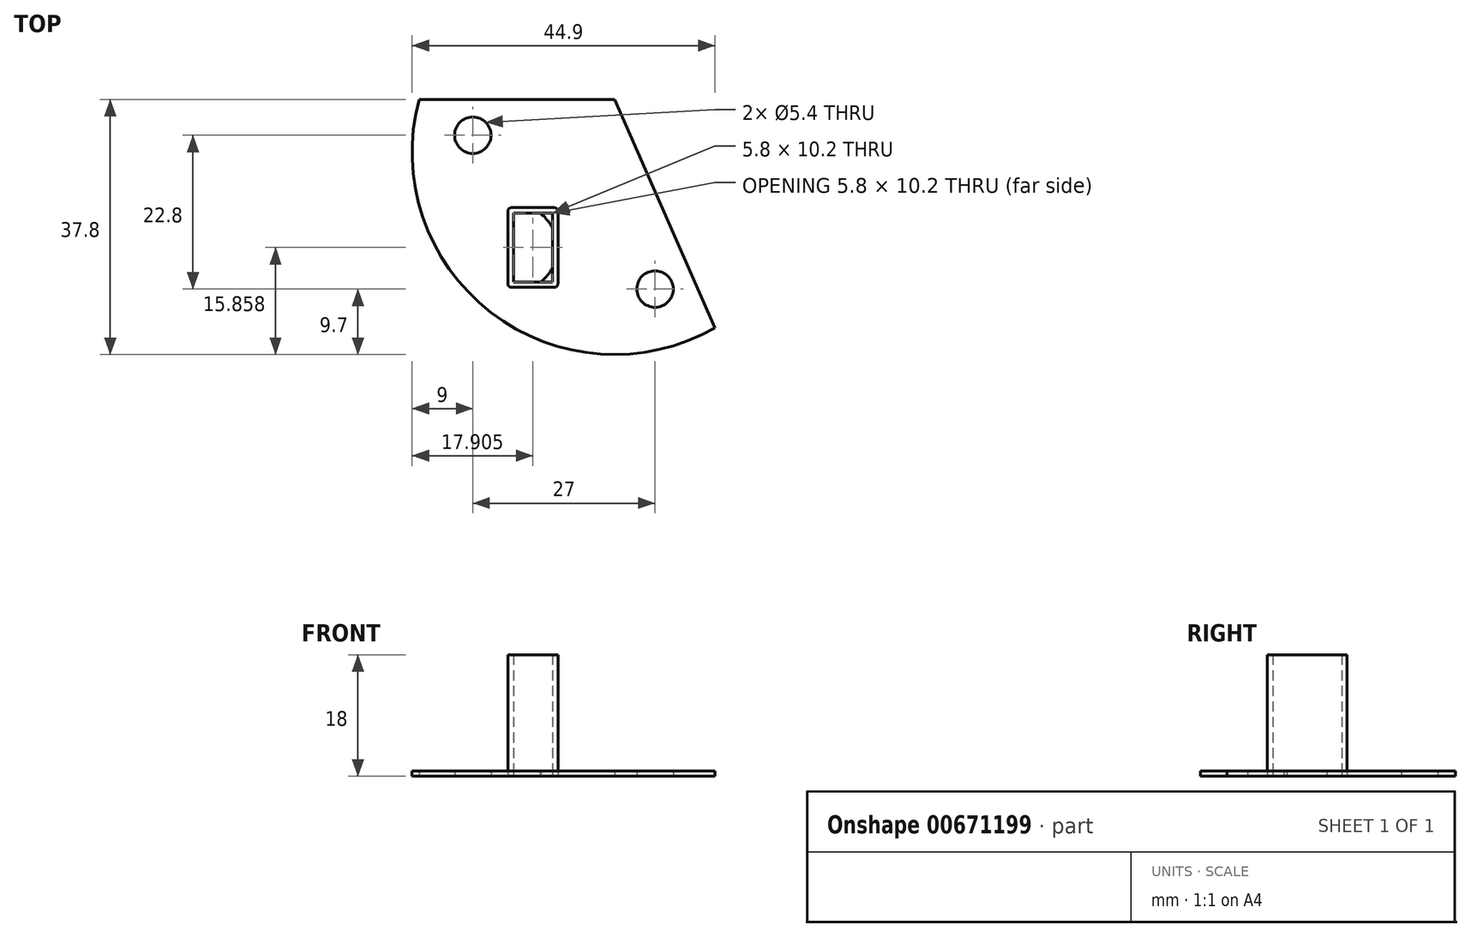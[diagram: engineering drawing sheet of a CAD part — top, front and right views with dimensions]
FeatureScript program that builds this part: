
annotation { "Feature Type Name" : "Feature", "Feature Type Description" : "" }
export const myFeature = defineFeature(function(context is Context, id is Id, definition is map)
    precondition{}
    {
        {
            var Q0;
            Q0=qCreatedBy(makeId("Top.planeOp"),FACE);
            var sketch = newSketch(context, id + "F0", { "sketchPlane" : qUnion([Q0])});
            skArc(sketch, "E0", {"start": v(-28.97, 7.8) * mm, "mid": v(-18.32, -23.75) * mm, "end": v(14.9, -26.04) * mm});
            skCircle(sketch, "E1", {"center": v(-21, 2.5) * mm, "radius": 2.7 * mm});
            skCircle(sketch, "E2", {"center": v(6, -20.3) * mm, "radius": 2.7 * mm});
            skCircle(sketch, "E3", {"center": v(-15, -14.2) * mm, "radius": 6.5 * mm});
            skLineSegment(sketch, "E4", {"start": v(-28.97, 7.8) * mm, "end": v(0, 7.8) * mm});
            skLineSegment(sketch, "E5", {"start": v(0, 7.8) * mm, "end": v(14.9, -26.04) * mm});
            skLineSegment(sketch, "E6.bottom", {"start": v(-15, -9.04) * mm, "end": v(-9.2, -9.04) * mm});
            skLineSegment(sketch, "E6.top", {"start": v(-15, -19.24) * mm, "end": v(-9.2, -19.24) * mm});
            skLineSegment(sketch, "E6.left", {"start": v(-15, -9.04) * mm, "end": v(-15, -19.24) * mm});
            skLineSegment(sketch, "E6.right", {"start": v(-9.2, -9.04) * mm, "end": v(-9.2, -19.24) * mm});
            skLineSegment(sketch, "E7.0", {"start": v(-8.4, -8.74) * mm, "end": v(-8.4, -19.54) * mm});
            skLineSegment(sketch, "E7.1", {"start": v(-15.3, -8.24) * mm, "end": v(-8.9, -8.24) * mm});
            skLineSegment(sketch, "E7.2", {"start": v(-15.8, -8.74) * mm, "end": v(-15.8, -19.54) * mm});
            skLineSegment(sketch, "E7.3", {"start": v(-15.3, -20.04) * mm, "end": v(-8.9, -20.04) * mm});
            skPoint(sketch, "E8.visualSharp", {"position": v(-15.8, -8.24) * mm});
            skArc(sketch, "E8.filletArc", {"start": v(-15.3, -8.24) * mm, "mid": v(-15.65, -8.39) * mm, "end": v(-15.8, -8.74) * mm});
            skPoint(sketch, "E9.visualSharp", {"position": v(-15.8, -20.04) * mm});
            skArc(sketch, "E9.filletArc", {"start": v(-15.8, -19.54) * mm, "mid": v(-15.65, -19.9) * mm, "end": v(-15.3, -20.04) * mm});
            skPoint(sketch, "E10.visualSharp", {"position": v(-8.4, -20.04) * mm});
            skArc(sketch, "E10.filletArc", {"start": v(-8.9, -20.04) * mm, "mid": v(-8.54, -19.9) * mm, "end": v(-8.4, -19.54) * mm});
            skPoint(sketch, "E11.visualSharp", {"position": v(-8.4, -8.24) * mm});
            skArc(sketch, "E11.filletArc", {"start": v(-8.4, -8.74) * mm, "mid": v(-8.54, -8.39) * mm, "end": v(-8.9, -8.24) * mm});
            skSolve(sketch);
        }
        {
            var Q0;
            Q0=makeQuery(id+"F0.imprint","IMPRINT",FACE,{"disambiguationData":[TD([[makeQuery(id+"F0.imprint","IMPRINT",EDGE,{"derivedFrom":sQuery(id+"F0.wireOp",EDGE,"E0")}),1.0]])]});
            var Q1;
            Q1=makeQuery(id+"F0.imprint","IMPRINT",FACE,{"disambiguationData":[TD([[makeQuery(id+"F0.imprint","IMPRINT",EDGE,{"derivedFrom":sQuery(id+"F0.wireOp",EDGE,"E7.2")}),-1.0]])]});
            var Q2;
            {var subQ0=sQuery(id+"F0.wireOp",EDGE,"E6.left");Q2=makeQuery(id+"F0.imprint","IMPRINT",FACE,{"disambiguationData":[TD([[makeQuery(id+"F0.imprint","IMPRINT",EDGE,{"derivedFrom":subQ0}),-1.0]])]});}
            var Q3;
            Q3=makeQuery(id+"F0.imprint","IMPRINT",FACE,{"disambiguationData":[TD([[makeQuery(id+"F0.imprint","IMPRINT",EDGE,{"derivedFrom":sQuery(id+"F0.wireOp",EDGE,"E7.0")}),-1.0]])]});
            var Q4;
            {var subQ0=sQuery(id+"F0.wireOp",EDGE,"E6.bottom");var subQ1=sQuery(id+"F0.wireOp",EDGE,"E3");var subQ2=makeQuery(id+"F0.imprint","INTERSECT",VERTEX,{"derivedFrom":[subQ1,subQ0]});Q4=makeQuery(id+"F0.imprint","IMPRINT",FACE,{"disambiguationData":[TD([[makeQuery(id+"F0.imprint","IMPRINT",EDGE,{"disambiguationData":[TD([[subQ2,1.0]])],"derivedFrom":subQ1}),-1.0]])]});}
            var Q5;
            {var subQ0=sQuery(id+"F0.wireOp",EDGE,"E6.right");var subQ1=sQuery(id+"F0.wireOp",EDGE,"E3");var subQ2=makeQuery(id+"F0.imprint","INTERSECT",VERTEX,{"disambiguationData":[OD(0.0)],"derivedFrom":[subQ1,subQ0]});Q5=makeQuery(id+"F0.imprint","IMPRINT",FACE,{"disambiguationData":[TD([[makeQuery(id+"F0.imprint","IMPRINT",EDGE,{"disambiguationData":[TD([[subQ2,1.0]])],"derivedFrom":subQ1}),1.0]])]});}
            var Q6;
            {var subQ0=sQuery(id+"F0.wireOp",EDGE,"E6.top");var subQ1=sQuery(id+"F0.wireOp",EDGE,"E3");var subQ2=makeQuery(id+"F0.imprint","INTERSECT",VERTEX,{"derivedFrom":[subQ1,subQ0]});Q6=makeQuery(id+"F0.imprint","IMPRINT",FACE,{"disambiguationData":[TD([[makeQuery(id+"F0.imprint","IMPRINT",EDGE,{"disambiguationData":[TD([[subQ2,-1.0]])],"derivedFrom":subQ1}),-1.0]])]});}
            extrude(context, id + "F1", {"entities" : qUnion([Q0, Q1, Q2, Q3, Q4, Q5, Q6]), "depth" : 0.8 * mm, "offsetDistance" : 25 * mm});
        }
        {
            var Q0;
            {var subQ0=sQuery(id+"F0.wireOp",EDGE,"E6.left");Q0=makeQuery(id+"F0.imprint","IMPRINT",FACE,{"disambiguationData":[TD([[makeQuery(id+"F0.imprint","IMPRINT",EDGE,{"derivedFrom":subQ0}),-1.0]])]});}
            var Q1;
            Q1=makeQuery(id+"F0.imprint","IMPRINT",FACE,{"disambiguationData":[TD([[makeQuery(id+"F0.imprint","IMPRINT",EDGE,{"derivedFrom":sQuery(id+"F0.wireOp",EDGE,"E7.0")}),-1.0]])]});
            var Q2;
            {var subQ0=sQuery(id+"F0.wireOp",EDGE,"E6.right");var subQ1=sQuery(id+"F0.wireOp",EDGE,"E3");var subQ2=makeQuery(id+"F0.imprint","INTERSECT",VERTEX,{"disambiguationData":[OD(0.0)],"derivedFrom":[subQ1,subQ0]});Q2=makeQuery(id+"F0.imprint","IMPRINT",FACE,{"disambiguationData":[TD([[makeQuery(id+"F0.imprint","IMPRINT",EDGE,{"disambiguationData":[TD([[subQ2,1.0]])],"derivedFrom":subQ1}),1.0]])]});}
            extrude(context, id + "F2", {"entities" : qUnion([Q0, Q1, Q2]), "depth" : 18 * mm, "offsetDistance" : 25 * mm});
        }
    });
